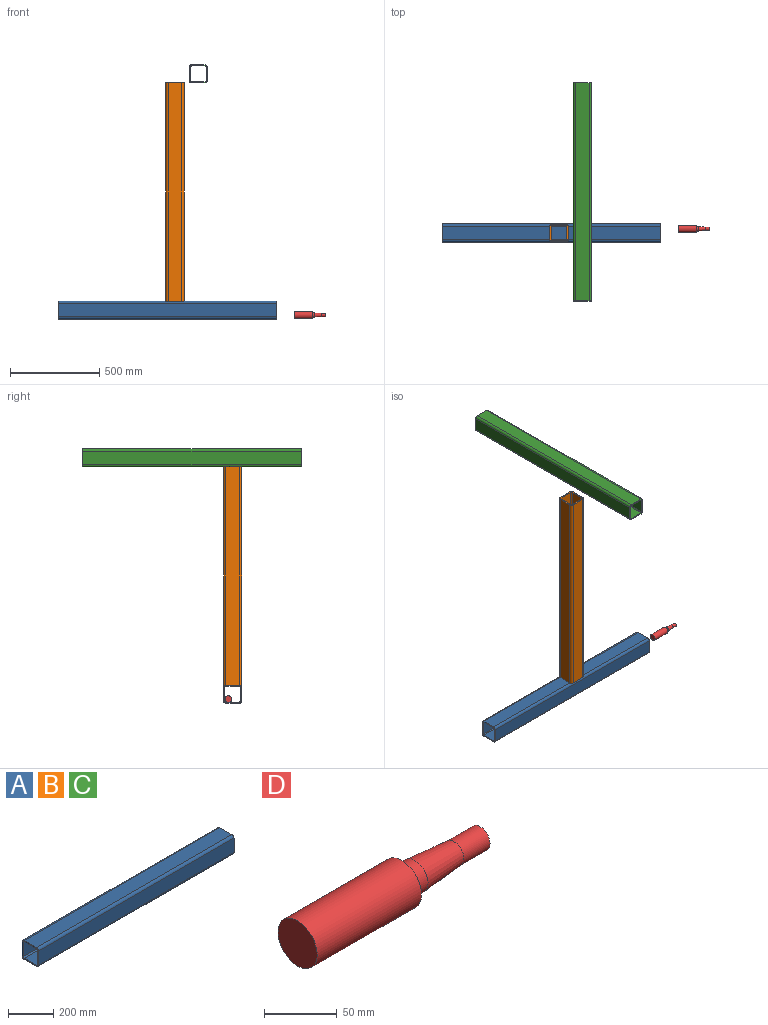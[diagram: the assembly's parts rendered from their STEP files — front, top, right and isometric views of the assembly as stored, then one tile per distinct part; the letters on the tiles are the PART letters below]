
ASSEMBLY  parts=4 mates=3
PART A: 18 faces, bbox 1219.2x101.6x101.6 mm
  f0: plane 1219.2x76.2mm, normal (0,1,0), area 92903mm2, adj f1,f15,f16,f17
  f1: cylinder r=12.7mm len=1219.2mm, axis (-1,0,0), area 24322mm2, adj f0,f2,f16,f17
  f2: plane 1219.2x76.2mm, normal (0,0,1), area 92903mm2, adj f1,f3,f16,f17
  f3: cylinder r=12.7mm len=1219.2mm, axis (-1,0,0), area 24322mm2, adj f2,f4,f16,f17
  f4: plane 1219.2x76.2mm, normal (0,-1,0), area 92903mm2, adj f3,f5,f16,f17
  f5: cylinder r=12.7mm len=1219.2mm, axis (-1,0,0), area 24322mm2, adj f4,f6,f16,f17
  f6: plane 1219.2x76.2mm, normal (0,0,-1), area 92903mm2, adj f5,f15,f16,f17
  f7: cylinder r=6.35mm len=1219.2mm, axis (-1,0,0), area 12161mm2, adj f8,f14,f16,f17
  f8: plane 1219.2x76.2mm, normal (0,-1,0), area 92903mm2, adj f7,f9,f16,f17
  f9: cylinder r=6.35mm len=1219.2mm, axis (-1,0,0), area 12161mm2, adj f8,f10,f16,f17
  f10: plane 1219.2x76.2mm, normal (0,0,1), area 92903mm2, adj f9,f11,f16,f17
  f11: cylinder r=6.35mm len=1219.2mm, axis (-1,0,0), area 12161mm2, adj f10,f12,f16,f17
  f12: plane 1219.2x76.2mm, normal (0,1,0), area 92903mm2, adj f11,f13,f16,f17
  f13: cylinder r=6.35mm len=1219.2mm, axis (-1,0,0), area 12161mm2, adj f12,f14,f16,f17
  f14: plane 1219.2x76.2mm, normal (0,0,-1), area 92903mm2, adj f7,f13,f16,f17
  f15: cylinder r=12.7mm len=1219.2mm, axis (-1,0,0), area 24322mm2, adj f0,f6,f16,f17
  f16: plane 101.6x101.6mm, normal (1,0,0), area 2315.5mm2, adj f0,f1,f2,f3,f4,f5,f6,f7
  f17: plane 101.6x101.6mm, normal (-1,0,0), area 2315.5mm2, adj f0,f1,f2,f3,f4,f5,f6,f7
PART B: same geometry as A
PART C: same geometry as A
PART D: 7 faces, bbox 177.8x38.1x38.1 mm
  f0: plane 38.1x38.1mm, normal (-1,0,0), area 1140.1mm2, adj f6
  f1: plane 19.05x19.05mm, normal (1,0,0), area 285mm2, adj f2
  f2: cylinder r=9.53mm len=25.4mm, axis (1,0,0), area 1520.1mm2, adj f1,f3
  f3: cone r=12.7mm half-angle=4.8deg, axis (-1,0,0), area 2669.4mm2, adj f2,f4
  f4: cylinder r=12.7mm len=25.4mm, axis (1,0,0), area 1013.4mm2, adj f3,f5
  f5: plane 38.1x38.1mm, normal (1,0,0), area 633.4mm2, adj f4,f6
  f6: cylinder r=19.05mm len=101.6mm, axis (1,0,0), area 12161mm2, adj f0,f5
PLACE A t=(-0.92,-28.61,-94.64)mm fixed
PLACE B rot(axis=(-0.71,0,-0.71),180deg) t=(43.53,-28.61,565.76)mm
PLACE C rot(axis=(0,0,-1),90deg) t=(173.55,198.59,1226.16)mm
PLACE D rot(axis=(1,0,0),90deg) t=(789.25,-25.55,-122.93)mm
MATE planar B.f16 <-> C.f6  axis (0,0,1) through (43.53,-28.61,1175.36)mm
MATE fastened B.f17 <-> A.f2  axis (0,0,-1) through (-0.92,-66.71,-43.84)mm
MATE planar A.f16 <-> D.f2  axis (1,0,0) through (608.68,-28.61,-50.19)mm
